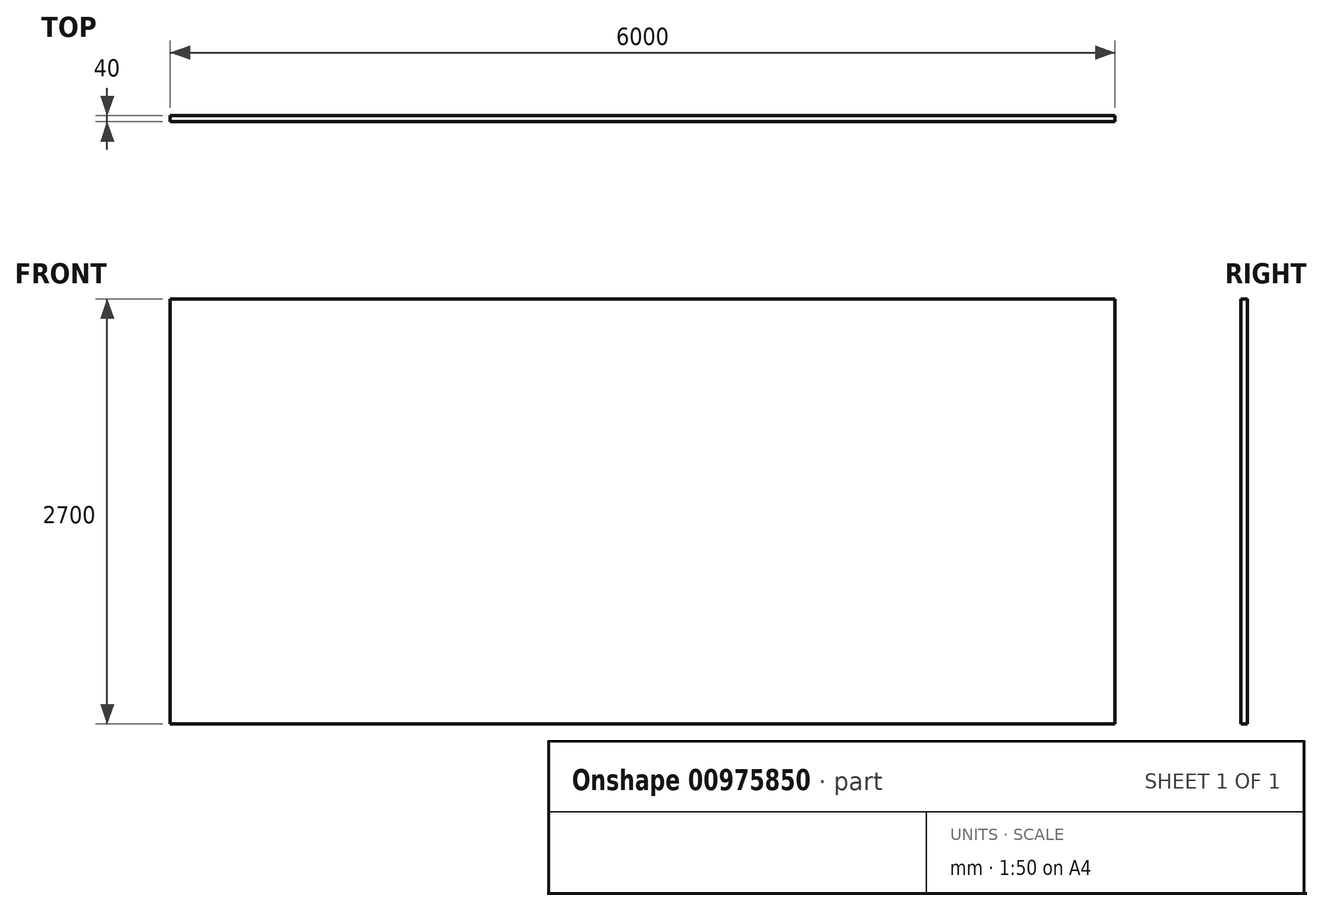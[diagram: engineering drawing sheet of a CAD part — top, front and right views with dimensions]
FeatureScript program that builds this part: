
annotation { "Feature Type Name" : "Feature", "Feature Type Description" : "" }
export const myFeature = defineFeature(function(context is Context, id is Id, definition is map)
    precondition{}
    {
        {
            var Q0;
            Q0=qCreatedBy(makeId("Front.planeOp"),FACE);
            var sketch = newSketch(context, id + "F0", { "sketchPlane" : qUnion([Q0])});
            skLineSegment(sketch, "E0.bottom", {"start": v(-3001.8, 1186.13) * mm, "end": v(2998.2, 1186.13) * mm});
            skLineSegment(sketch, "E0.top", {"start": v(-3001.8, -1513.87) * mm, "end": v(2998.2, -1513.87) * mm});
            skLineSegment(sketch, "E0.left", {"start": v(-3001.8, 1186.13) * mm, "end": v(-3001.8, -1513.87) * mm});
            skLineSegment(sketch, "E0.right", {"start": v(2998.2, 1186.13) * mm, "end": v(2998.2, -1513.87) * mm});
            skSolve(sketch);
        }
        {
            var Q0;
            Q0=makeQuery(id+"F0.imprint","IMPRINT",FACE,{"disambiguationData":[TD([[makeQuery(id+"F0.imprint","IMPRINT",EDGE,{"derivedFrom":sQuery(id+"F0.wireOp",EDGE,"E0.bottom")}),-1.0]])]});
            extrude(context, id + "F1", {"entities" : qUnion([Q0]), "depth" : 40 * mm, "offsetDistance" : 25 * mm});
        }
    });
